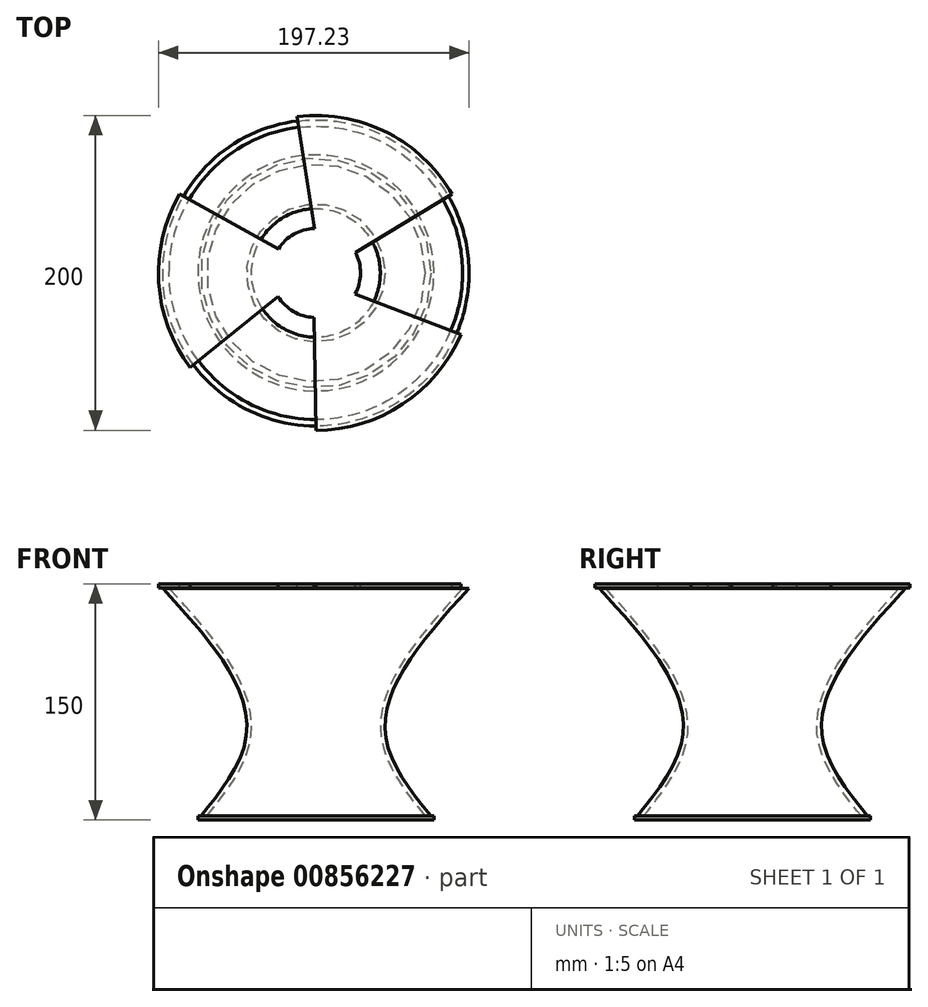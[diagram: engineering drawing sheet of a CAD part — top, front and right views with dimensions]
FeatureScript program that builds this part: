
annotation { "Feature Type Name" : "Feature", "Feature Type Description" : "" }
export const myFeature = defineFeature(function(context is Context, id is Id, definition is map)
    precondition{}
    {
        {
            var Q0;
            Q0=qCreatedBy(makeId("Top.planeOp"),FACE);
            var sketch = newSketch(context, id + "F0", { "sketchPlane" : qUnion([Q0])});
            skCircle(sketch, "E0", {"center": v(0, 0) * mm, "radius": 100 * mm});
            skSolve(sketch);
        }
        {
            var Q0;
            Q0=qCreatedBy(makeId("Top.planeOp"),FACE);
            cPlane(context, id + "F1", {"entities" : qUnion([Q0]), "cplaneType" : CPlaneType.OFFSET, "offset" : 100 * mm, "oppositeDirection" : true, "width" : 150 * mm, "height" : 150 * mm});
        }
        {
            var Q0;
            Q0=qCreatedBy(id+"F1.planeOp",FACE);
            var sketch = newSketch(context, id + "F2", { "sketchPlane" : qUnion([Q0])});
            skCircle(sketch, "E1", {"center": v(0, 0) * mm, "radius": 44.82 * mm});
            skSolve(sketch);
        }
        {
            var Q0;
            Q0=qCreatedBy(id+"F1.planeOp",FACE);
            cPlane(context, id + "F3", {"entities" : qUnion([Q0]), "cplaneType" : CPlaneType.OFFSET, "offset" : 50 * mm, "oppositeDirection" : true, "width" : 150 * mm, "height" : 150 * mm});
        }
        {
            var Q0;
            Q0=qCreatedBy(id+"F3.planeOp",FACE);
            var sketch = newSketch(context, id + "F4", { "sketchPlane" : qUnion([Q0])});
            skCircle(sketch, "E2", {"center": v(0, 0) * mm, "radius": 75 * mm});
            skSolve(sketch);
        }
        {
            var Q0;
            Q0=makeQuery(id+"F0.imprint","IMPRINT",FACE,{"disambiguationData":[TD([[makeQuery(id+"F0.imprint","IMPRINT",EDGE,{"derivedFrom":sQuery(id+"F0.wireOp",EDGE,"E0")}),1.0]])]});
            var Q1;
            Q1=makeQuery(id+"F2.imprint","IMPRINT",FACE,{"disambiguationData":[TD([[makeQuery(id+"F2.imprint","IMPRINT",EDGE,{"derivedFrom":sQuery(id+"F2.wireOp",EDGE,"E1")}),1.0]])]});
            var Q2;
            Q2=makeQuery(id+"F4.imprint","IMPRINT",FACE,{"disambiguationData":[TD([[makeQuery(id+"F4.imprint","IMPRINT",EDGE,{"derivedFrom":sQuery(id+"F4.wireOp",EDGE,"E2")}),1.0]])]});
            loft(context, id + "F5", {"sheetProfilesArray" : [{ "sheetProfileEntities" : qUnion([Q0]) }, { "sheetProfileEntities" : qUnion([Q1]) }, { "sheetProfileEntities" : qUnion([Q2]) }]});
        }
        {
            var Q0;
            Q0=makeQuery(id+"F5.opLoft","CAP_FACE",FACE,{"disambiguationData":[OSD([makeQuery(id+"F4.imprint","IMPRINT",FACE,{"disambiguationData":[TD([[makeQuery(id+"F4.imprint","IMPRINT",EDGE,{"derivedFrom":sQuery(id+"F4.wireOp",EDGE,"E2")}),1.0]])]})])],"isStart":true});
            shell(context, id + "F6", {"entities" : qUnion([Q0]), "thickness" : 3 * mm});
        }
        {
            var Q0;
            Q0=makeQuery(id+"F5.opLoft","CAP_FACE",FACE,{"disambiguationData":[OSD([makeQuery(id+"F0.imprint","IMPRINT",FACE,{"disambiguationData":[TD([[makeQuery(id+"F0.imprint","IMPRINT",EDGE,{"derivedFrom":sQuery(id+"F0.wireOp",EDGE,"E0")}),1.0]])]})])],"isStart":true});
            extrude(context, id + "F7", {"entities" : qUnion([Q0]), "operationType" : NewBodyOperationType.REMOVE, "oppositeDirection" : true, "depth" : 3 * mm, "offsetDistance" : 25 * mm});
        }
        {
            var Q0;
            Q0=qCreatedBy(id+"F3.planeOp",FACE);
            var sketch = newSketch(context, id + "F8", { "sketchPlane" : qUnion([Q0])});
            skCircle(sketch, "E3", {"center": v(0, 0) * mm, "radius": 75 * mm});
            skSolve(sketch);
        }
        {
            var Q0;
            Q0 = qSketchRegion(id + "F8", true);
            extrude(context, id + "F9", {"entities" : qUnion([Q0]), "operationType" : NewBodyOperationType.ADD, "depth" : 2.5 * mm, "offsetDistance" : 25 * mm});
        }
        {
            var Q0;
            Q0=qCreatedBy(id+"F3.planeOp",FACE);
            cPlane(context, id + "F10", {"entities" : qUnion([Q0]), "cplaneType" : CPlaneType.OFFSET, "offset" : 150 * mm, "width" : 150 * mm, "height" : 150 * mm});
        }
        {
            var Q0;
            Q0=qCreatedBy(id+"F10.planeOp",FACE);
            var sketch = newSketch(context, id + "F11", { "sketchPlane" : qUnion([Q0])});
            skCircle(sketch, "E4", {"center": v(0, 0) * mm, "radius": 100 * mm});
            skArc(sketch, "E5", {"start": v(97.42, 22.58) * mm, "mid": v(80.13, 59.61) * mm, "end": v(49.64, 86.81) * mm});
            skCircle(sketch, "E6", {"center": v(0, 0) * mm, "radius": 28.33 * mm});
            skLineSegment(sketch, "E7", {"start": v(-24.06, -14.95) * mm, "end": v(-79.93, -60.1) * mm});
            skLineSegment(sketch, "E8", {"start": v(-1.22, -28.3) * mm, "end": v(0, -100) * mm});
            skLineSegment(sketch, "E9.1.0", {"start": v(25.12, 13.1) * mm, "end": v(86.6, 50) * mm});
            skLineSegment(sketch, "E9.1.1", {"start": v(24.98, -13.36) * mm, "end": v(92, -39.18) * mm});
            skLineSegment(sketch, "E9.2.0", {"start": v(-23.9, 15.2) * mm, "end": v(-86.6, 50) * mm});
            skLineSegment(sketch, "E9.2.1", {"start": v(-0.92, 28.31) * mm, "end": v(-12.07, 99.27) * mm});
            skSolve(sketch);
        }
        {
            var Q0;
            {var subQ5=sQuery(id+"F11.wireOp",EDGE,"E9.2.1");Q0=makeQuery(id+"F11.imprint","IMPRINT",FACE,{"disambiguationData":[TD([[makeQuery(id+"F11.imprint","IMPRINT",EDGE,{"derivedFrom":subQ5}),-1.0]])]});}
            var Q1;
            {var subQ0=sQuery(id+"F11.wireOp",EDGE,"E8");Q1=makeQuery(id+"F11.imprint","IMPRINT",FACE,{"disambiguationData":[TD([[makeQuery(id+"F11.imprint","IMPRINT",EDGE,{"derivedFrom":subQ0}),1.0]])]});}
            var Q2;
            {var subQ0=sQuery(id+"F11.wireOp",EDGE,"E7");Q2=makeQuery(id+"F11.imprint","IMPRINT",FACE,{"disambiguationData":[TD([[makeQuery(id+"F11.imprint","IMPRINT",EDGE,{"derivedFrom":subQ0}),-1.0]])]});}
            var Q3;
            {var subQ0=sQuery(id+"F11.wireOp",EDGE,"E6");var subQ5=makeQuery(id+"F11.imprint","INTERSECT",VERTEX,{"derivedFrom":[subQ0,sQuery(id+"F11.wireOp",EDGE,"E9.1.0")]});Q3=makeQuery(id+"F11.imprint","IMPRINT",FACE,{"disambiguationData":[TD([[makeQuery(id+"F11.imprint","IMPRINT",EDGE,{"disambiguationData":[TD([[subQ5,-1.0]])],"derivedFrom":subQ0}),1.0]])]});}
            extrude(context, id + "F12", {"entities" : qUnion([Q0, Q1, Q2, Q3]), "operationType" : NewBodyOperationType.ADD, "oppositeDirection" : true, "depth" : 2.5 * mm, "offsetDistance" : 25 * mm});
        }
    });
